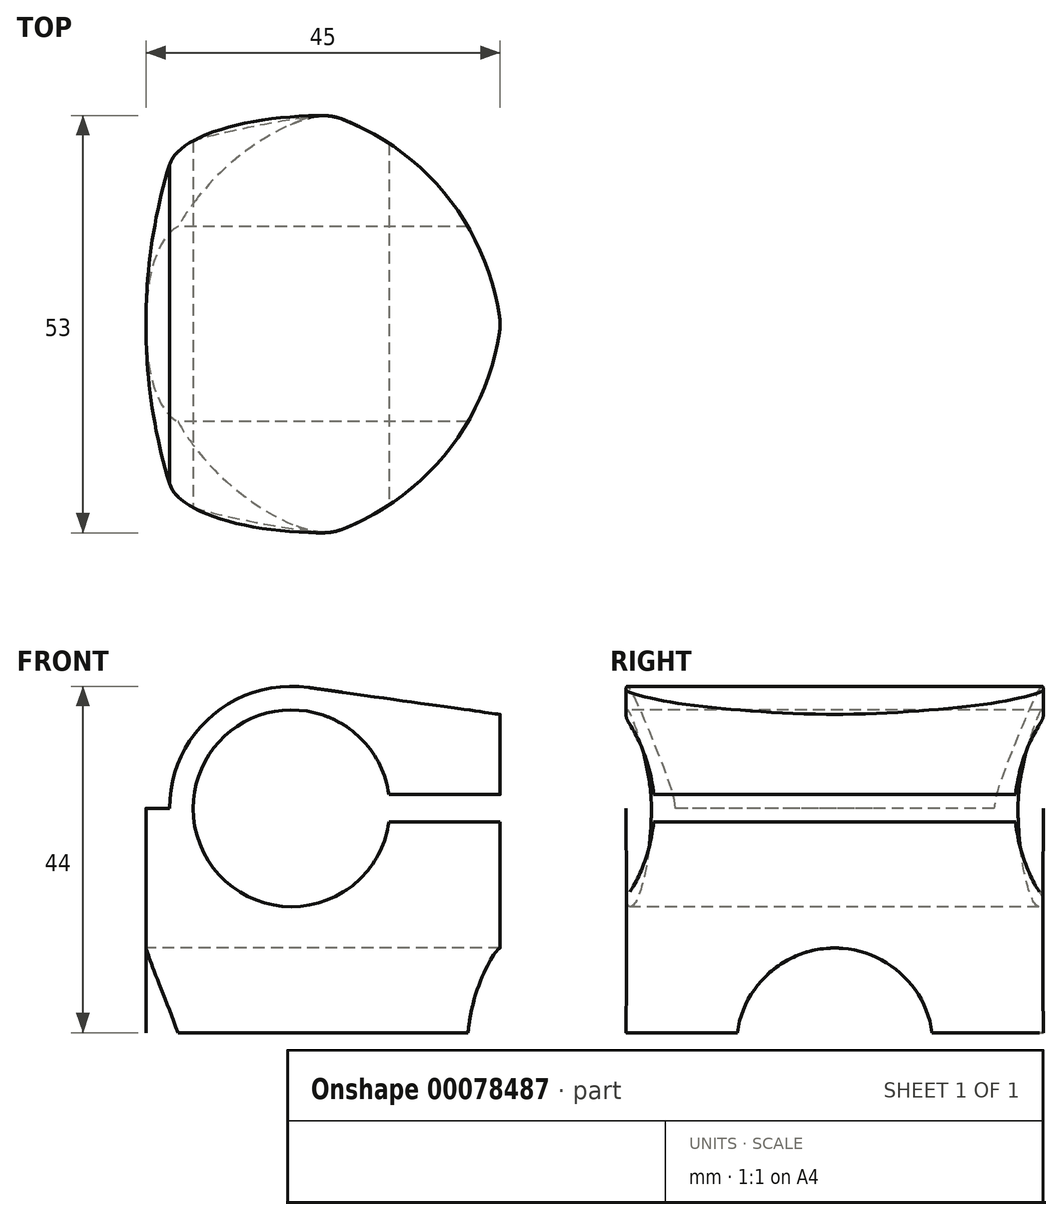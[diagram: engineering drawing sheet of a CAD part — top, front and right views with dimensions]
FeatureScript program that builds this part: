
annotation { "Feature Type Name" : "Feature", "Feature Type Description" : "" }
export const myFeature = defineFeature(function(context is Context, id is Id, definition is map)
    precondition{}
    {
        {
            var Q0;
            Q0=qCreatedBy(makeId("Top.planeOp"),FACE);
            var sketch = newSketch(context, id + "F0", { "sketchPlane" : qUnion([Q0])});
            skArc(sketch, "E0", {"start": v(22.42, -1.04) * mm, "mid": v(22.5, 0) * mm, "end": v(22.42, 1.04) * mm});
            skArc(sketch, "E1", {"start": v(-2.57, -26.01) * mm, "mid": v(0, -26.5) * mm, "end": v(2.57, -26.01) * mm});
            skLineSegment(sketch, "E2", {"start": v(0, 26.5) * mm, "end": v(0, -26.5) * mm, "construction": true});
            skArc(sketch, "E3.MirrorC", {"start": v(-22.42, -1.04) * mm, "mid": v(-22.5, 0) * mm, "end": v(-22.42, 1.04) * mm});
            skLineSegment(sketch, "E4", {"start": v(-22.5, 0) * mm, "end": v(22.5, 0) * mm, "construction": true});
            skArc(sketch, "E5.MirrorC", {"start": v(-2.57, 26.01) * mm, "mid": v(0, 26.5) * mm, "end": v(2.57, 26.01) * mm});
            skArc(sketch, "E6", {"start": v(2.57, -26.01) * mm, "mid": v(15.84, -16.18) * mm, "end": v(22.42, -1.04) * mm});
            skArc(sketch, "E7", {"start": v(22.42, 1.04) * mm, "mid": v(15.84, 16.18) * mm, "end": v(2.57, 26.01) * mm});
            skArc(sketch, "E8.MirrorCS", {"start": v(-2.57, -26.01) * mm, "mid": v(-15.84, -16.18) * mm, "end": v(-22.42, -1.04) * mm});
            skArc(sketch, "E9.MirrorCS", {"start": v(-22.42, 1.04) * mm, "mid": v(-15.84, 16.18) * mm, "end": v(-2.57, 26.01) * mm});
            skSolve(sketch);
        }
        {
            var Q0;
            Q0=qCreatedBy(makeId("Top.planeOp"),FACE);
            cPlane(context, id + "F1", {"entities" : qUnion([Q0]), "cplaneType" : CPlaneType.OFFSET, "offset" : 28.5 * mm, "width" : 150 * mm, "height" : 150 * mm});
        }
        {
            var Q0;
            Q0=qCreatedBy(id+"F1.planeOp",FACE);
            var sketch = newSketch(context, id + "F2", { "sketchPlane" : qUnion([Q0])});
            skLineSegment(sketch, "E10", {"start": v(0, 26.5) * mm, "end": v(0, -26.5) * mm, "construction": true});
            skLineSegment(sketch, "E11", {"start": v(22.5, 0) * mm, "end": v(-22.5, 0) * mm, "construction": true});
            skCircle(sketch, "E12", {"center": v(-15.5, 0) * mm, "radius": 7 * mm, "construction": true});
            skEllipticalArc(sketch, "E13", {});
            skEllipticalArc(sketch, "E14.MirrorC", {"construction": true});
            skArc(sketch, "E15", {"start": v(-19.5, 20.25) * mm, "mid": v(-21.35, 12.62) * mm, "end": v(-22.33, 4.82) * mm});
            skArc(sketch, "E16", {"start": v(0, 12.5) * mm, "mid": v(6.88, 18.2) * mm, "end": v(2.57, 26.01) * mm, "construction": true});
            skArc(sketch, "E17.MirrorC", {"start": v(0, -12.5) * mm, "mid": v(6.88, -18.2) * mm, "end": v(2.57, -26.01) * mm, "construction": true});
            skArc(sketch, "E18", {"start": v(22.42, 1.04) * mm, "mid": v(15.84, 16.18) * mm, "end": v(2.57, 26.01) * mm});
            skArc(sketch, "E19.MirrorCS", {"start": v(22.42, -1.04) * mm, "mid": v(15.84, -16.18) * mm, "end": v(2.57, -26.01) * mm});
            skEllipticalArc(sketch, "E20", {"construction": true});
            skArc(sketch, "E21", {"start": v(2.57, 26.01) * mm, "mid": v(1.3, 26.38) * mm, "end": v(0, 26.5) * mm});
            skEllipticalArc(sketch, "E22", {});
            skArc(sketch, "E23", {"start": v(2.57, -26.01) * mm, "mid": v(1.3, -26.38) * mm, "end": v(0, -26.5) * mm});
            skArc(sketch, "E24", {"start": v(22.42, 1.04) * mm, "mid": v(8.5, 0) * mm, "end": v(22.42, -1.04) * mm, "construction": true});
            skArc(sketch, "E25", {"start": v(22.42, -1.04) * mm, "mid": v(22.5, 0) * mm, "end": v(22.42, 1.04) * mm});
            skArc(sketch, "E26", {"start": v(-22.33, 4.82) * mm, "mid": v(-22.5, 0) * mm, "end": v(-22.33, -4.82) * mm});
            skArc(sketch, "E27", {"start": v(-22.33, -4.82) * mm, "mid": v(-21.35, -12.62) * mm, "end": v(-19.5, -20.25) * mm});
            const initialGuessF2  = {"E13": [0, 0.0195, -1, 0, 0.01961361710055867, 0.007, 4.71238898038469, 6.17549716794503], "E14.MirrorC": [0, -0.0195, -1, 0, 0.01961361710055867, 0.007, 4.71238898038469, 0.10768813923455606], "E20": [0, 0.0195, -1, 0, 0.01961361710055867, 0.007, 6.17549716794503, 1.5707963267948966], "E22": [0, -0.0195, -1, 0, 0.01961361710055867, 0.007, 0.10768813923455606, 1.5707963267948966]};
            skSetInitialGuess(sketch, initialGuessF2);
            skSolve(sketch);
        }
        {
            var Q0;
            Q0=makeQuery(id+"F2.imprint","IMPRINT",FACE,{"disambiguationData":[TD([[makeQuery(id+"F2.imprint","IMPRINT",EDGE,{"derivedFrom":sQuery(id+"F2.wireOp",EDGE,"E13")}),1.0]])]});
            var Q1;
            Q1=makeQuery(id+"F0.imprint","IMPRINT",FACE,{"disambiguationData":[TD([[makeQuery(id+"F0.imprint","IMPRINT",EDGE,{"derivedFrom":sQuery(id+"F0.wireOp",EDGE,"E0")}),1.0]])]});
            loft(context, id + "F3", {"startCondition" : LoftEndDerivativeType.NORMAL_TO_PROFILE, "startMagnitude" : 1, "sheetProfilesArray" : [{ "sheetProfileEntities" : qUnion([Q0]) }, { "sheetProfileEntities" : qUnion([Q1]) }]});
        }
        {
            var Q0;
            Q0=sQuery(id+"F0.wireOp",VERTEX,"E4.start");
            var Q1;
            Q1=sQuery(id+"F0.wireOp",EDGE,"E4");
            cPlane(context, id + "F4", {"entities" : qUnion([Q0, Q1]), "cplaneType" : CPlaneType.LINE_POINT, "offset" : 150 * mm, "width" : 150 * mm, "height" : 150 * mm});
        }
        {
            var Q0;
            Q0=qCreatedBy(id+"F4.planeOp",FACE);
            var sketch = newSketch(context, id + "F5", { "sketchPlane" : qUnion([Q0])});
            skLineSegment(sketch, "E28", {"start": v(0, -11.04) * mm, "end": v(0, 30.21) * mm, "construction": true});
            skCircle(sketch, "E29", {"center": v(0, -1.75) * mm, "radius": 12.5 * mm});
            skSolve(sketch);
        }
        {
            var Q0;
            Q0=makeQuery(id+"F5.imprint","IMPRINT",FACE,{"disambiguationData":[TD([[makeQuery(id+"F5.imprint","IMPRINT",EDGE,{"derivedFrom":sQuery(id+"F5.wireOp",EDGE,"E29")}),1.0]])]});
            extrude(context, id + "F6", {"entities" : qUnion([Q0]), "operationType" : NewBodyOperationType.REMOVE, "endBound" : BoundingType.THROUGH_ALL, "depth" : 25 * mm});
        }
        {
            var Q0;
            Q0=sQuery(id+"F0.wireOp",VERTEX,"E2.end");
            var Q1;
            Q1=sQuery(id+"F0.wireOp",EDGE,"E2");
            cPlane(context, id + "F7", {"entities" : qUnion([Q0, Q1]), "cplaneType" : CPlaneType.LINE_POINT, "offset" : 150 * mm, "width" : 150 * mm, "height" : 150 * mm});
        }
        {
            var Q0;
            Q0=qCreatedBy(id+"F7.planeOp",FACE);
            var sketch = newSketch(context, id + "F8", { "sketchPlane" : qUnion([Q0])});
            skLineSegment(sketch, "E30", {"start": v(-44.09, 28.5) * mm, "end": v(50.48, 28.5) * mm, "construction": true});
            skCircle(sketch, "E31", {"center": v(-4, 28.5) * mm, "radius": 12.5 * mm});
            skPoint(sketch, "E32", {"position": v(22.5, 28.5) * mm});
            skLineSegment(sketch, "E33", {"start": v(22.5, 40.43) * mm, "end": v(22.5, 30.25) * mm});
            skLineSegment(sketch, "E34", {"start": v(22.5, 30.25) * mm, "end": v(8.38, 30.25) * mm});
            skLineSegment(sketch, "E35", {"start": v(22.5, 40.43) * mm, "end": v(-1.84, 43.85) * mm});
            skLineSegment(sketch, "E36.MirrorCS", {"start": v(22.5, 26.75) * mm, "end": v(8.38, 26.75) * mm});
            skLineSegment(sketch, "E37", {"start": v(22.5, 30.25) * mm, "end": v(22.5, 26.75) * mm});
            skLineSegment(sketch, "E38.bottom", {"start": v(-27.81, 55.87) * mm, "end": v(35.64, 55.87) * mm});
            skLineSegment(sketch, "E38.left", {"start": v(-27.81, 55.87) * mm, "end": v(-27.81, 28.5) * mm});
            skLineSegment(sketch, "E38.right", {"start": v(35.64, 55.87) * mm, "end": v(35.64, 40.43) * mm});
            skLineSegment(sketch, "E39.trimOffspring", {"start": v(22.5, 40.43) * mm, "end": v(35.64, 40.43) * mm});
            skLineSegment(sketch, "E40", {"start": v(-19.5, 28.5) * mm, "end": v(-27.81, 28.5) * mm});
            skArc(sketch, "E41", {"start": v(-1.84, 43.85) * mm, "mid": v(-14.17, 40.2) * mm, "end": v(-19.5, 28.5) * mm});
            skArc(sketch, "E42", {"start": v(-19.5, 28.5) * mm, "mid": v(6.17, 16.8) * mm, "end": v(-1.84, 43.85) * mm});
            skPoint(sketch, "E43.orphan", {"position": v(11.4, 30.25) * mm});
            skPoint(sketch, "E44.orphan", {"position": v(11.4, 26.75) * mm});
            skSolve(sketch);
        }
        {
            var Q0;
            Q0=makeQuery(id+"F3.opLoft","CAP_FACE",FACE,{"disambiguationData":[OSD([makeQuery(id+"F2.imprint","IMPRINT",FACE,{"disambiguationData":[TD([[makeQuery(id+"F2.imprint","IMPRINT",EDGE,{"derivedFrom":sQuery(id+"F2.wireOp",EDGE,"E13")}),1.0]])]})])],"isStart":true});
            var sketch = newSketch(context, id + "F9", { "sketchPlane" : qUnion([Q0])});
            skLineSegment(sketch, "E45", {"start": v(-19.5, 36.34) * mm, "end": v(-19.5, -37.9) * mm});
            skSolve(sketch);
        }
        {
            var Q0;
            {var subQ0=sQuery(id+"F2.wireOp",EDGE,"E21");var subQ2=sQuery(id+"F2.wireOp",EDGE,"E13");var subQ8=sQuery(id+"F2.wireOp",EDGE,"E15");var subQ9=makeQuery(id+"F3.opLoft","MID_CAP_EDGE",EDGE,{"disambiguationData":[OSD([subQ2,subQ8,subQ0])],"capPos":0.0});Q0=makeQuery(id+"F9.imprint","IMPRINT",FACE,{"disambiguationData":[TD([[makeQuery(id+"F9.imprint","IMPRINT",EDGE,{"derivedFrom":subQ9}),1.0]])]});}
            extrude(context, id + "F10", {"entities" : qUnion([Q0]), "operationType" : NewBodyOperationType.ADD, "depth" : 25 * mm});
        }
        {
            var Q0;
            {var subQ0=sQuery(id+"F8.wireOp",EDGE,"E37");Q0=makeQuery(id+"F8.imprint","IMPRINT",FACE,{"disambiguationData":[TD([[makeQuery(id+"F8.imprint","IMPRINT",EDGE,{"derivedFrom":subQ0}),-1.0]])]});}
            var Q1;
            Q1=makeQuery(id+"F8.imprint","IMPRINT",FACE,{"disambiguationData":[TD([[makeQuery(id+"F8.imprint","IMPRINT",EDGE,{"derivedFrom":sQuery(id+"F8.wireOp",EDGE,"E35")}),-1.0]])]});
            var Q2;
            {var subQ0=sQuery(id+"F8.wireOp",EDGE,"E31");var subQ1=makeQuery(id+"F8.imprint","INTERSECT",VERTEX,{"derivedFrom":[subQ0,sQuery(id+"F8.wireOp",EDGE,"E34")]});Q2=makeQuery(id+"F8.imprint","IMPRINT",FACE,{"disambiguationData":[TD([[makeQuery(id+"F8.imprint","IMPRINT",EDGE,{"disambiguationData":[TD([[subQ1,-1.0]])],"derivedFrom":subQ0}),1.0]])]});}
            var Q3;
            {var subQ0=sQuery(id+"F8.wireOp",EDGE,"E34");var subQ1=sQuery(id+"F8.wireOp",EDGE,"E31");var subQ2=makeQuery(id+"F8.imprint","INTERSECT",VERTEX,{"derivedFrom":[subQ1,subQ0]});Q3=makeQuery(id+"F8.imprint","IMPRINT",FACE,{"disambiguationData":[TD([[makeQuery(id+"F8.imprint","IMPRINT",EDGE,{"disambiguationData":[TD([[subQ2,1.0]])],"derivedFrom":subQ1}),-1.0]])]});}
            extrude(context, id + "F11", {"entities" : qUnion([Q0, Q1, Q2, Q3]), "operationType" : NewBodyOperationType.REMOVE, "endBound" : BoundingType.THROUGH_ALL, "oppositeDirection" : true, "depth" : 25 * mm});
        }
    });
